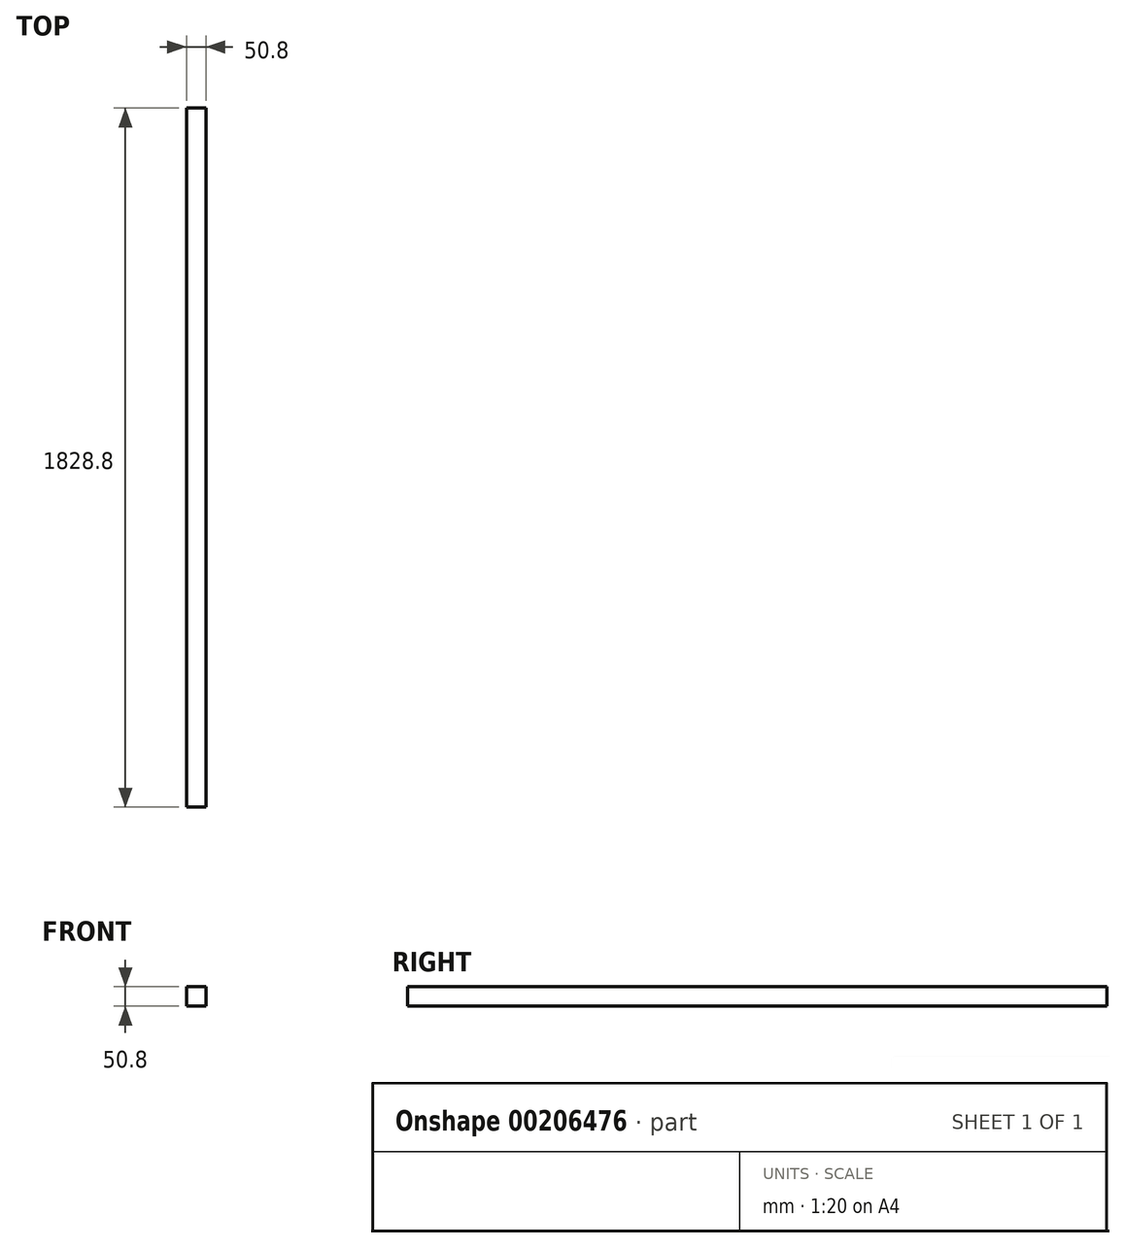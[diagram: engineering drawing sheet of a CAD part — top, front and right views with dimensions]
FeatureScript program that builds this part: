
annotation { "Feature Type Name" : "Feature", "Feature Type Description" : "" }
export const myFeature = defineFeature(function(context is Context, id is Id, definition is map)
    precondition{}
    {
        {
            var Q0;
            Q0=qCreatedBy(makeId("Front.planeOp"),FACE);
            var sketch = newSketch(context, id + "F0", { "sketchPlane" : qUnion([Q0])});
            skLineSegment(sketch, "E0.bottom", {"start": v(25.4, 25.4) * mm, "end": v(-25.4, 25.4) * mm});
            skLineSegment(sketch, "E0.top", {"start": v(25.4, -25.4) * mm, "end": v(-25.4, -25.4) * mm});
            skLineSegment(sketch, "E0.left", {"start": v(25.4, 25.4) * mm, "end": v(25.4, -25.4) * mm});
            skLineSegment(sketch, "E0.right", {"start": v(-25.4, 25.4) * mm, "end": v(-25.4, -25.4) * mm});
            skPoint(sketch, "E0.middle", {"position": v(0, 0) * mm});
            skSolve(sketch);
        }
        {
            var Q0;
            Q0 = qSketchRegion(id + "F0", true);
            extrude(context, id + "F1", {"entities" : qUnion([Q0]), "depth" : 1828.8 * mm});
        }
    });
